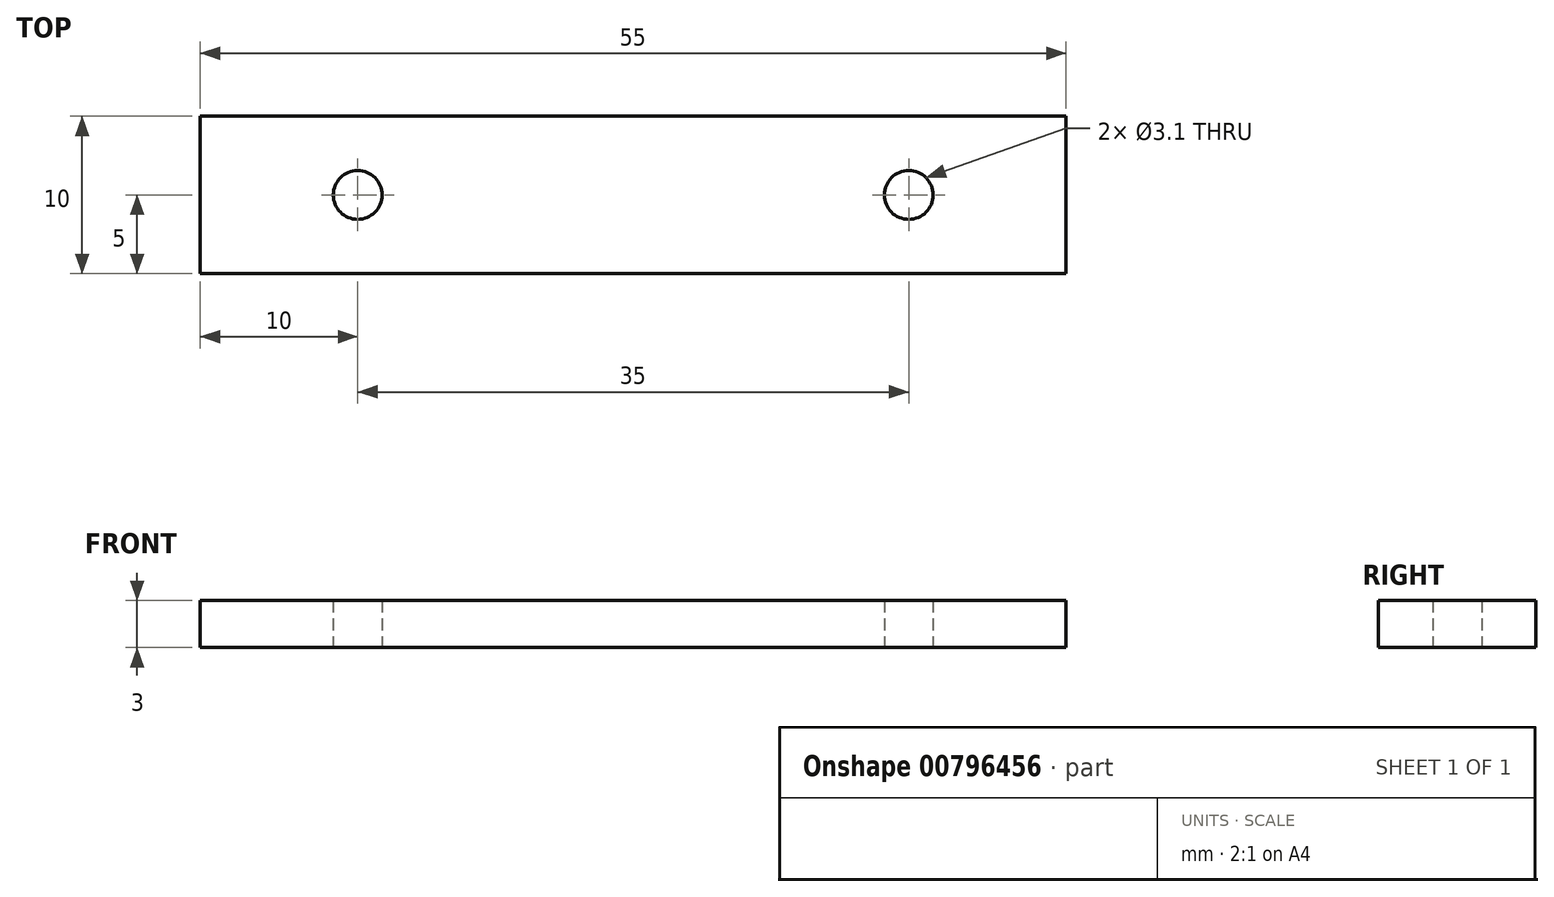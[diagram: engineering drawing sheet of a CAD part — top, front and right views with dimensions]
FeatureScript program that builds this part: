
annotation { "Feature Type Name" : "Feature", "Feature Type Description" : "" }
export const myFeature = defineFeature(function(context is Context, id is Id, definition is map)
    precondition{}
    {
        {
            var Q0;
            Q0=qCreatedBy(makeId("Top.planeOp"),FACE);
            var sketch = newSketch(context, id + "F0", { "sketchPlane" : qUnion([Q0])});
            skLineSegment(sketch, "E0.bottom", {"start": v(27.5, 5) * mm, "end": v(-27.5, 5) * mm});
            skLineSegment(sketch, "E0.top", {"start": v(27.5, -5) * mm, "end": v(-27.5, -5) * mm});
            skLineSegment(sketch, "E0.left", {"start": v(27.5, 5) * mm, "end": v(27.5, -5) * mm});
            skLineSegment(sketch, "E0.right", {"start": v(-27.5, 5) * mm, "end": v(-27.5, -5) * mm});
            skPoint(sketch, "E0.middle", {"position": v(0, 0) * mm});
            skLineSegment(sketch, "E1", {"start": v(-27.5, -5) * mm, "end": v(-17.5, -5) * mm, "construction": true});
            skCircle(sketch, "E2", {"center": v(-17.5, 0) * mm, "radius": 1.55 * mm});
            skLineSegment(sketch, "E3", {"start": v(27.5, -5) * mm, "end": v(17.5, -5) * mm, "construction": true});
            skCircle(sketch, "E4", {"center": v(17.5, 0) * mm, "radius": 1.55 * mm});
            skSolve(sketch);
        }
        {
            var Q0;
            Q0=makeQuery(id+"F0.imprint","IMPRINT",FACE,{"disambiguationData":[TD([[makeQuery(id+"F0.imprint","IMPRINT",EDGE,{"derivedFrom":sQuery(id+"F0.wireOp",EDGE,"E0.bottom")}),1.0]])]});
            extrude(context, id + "F1", {"entities" : qUnion([Q0]), "depth" : 3 * mm, "offsetDistance" : 25 * mm});
        }
    });
